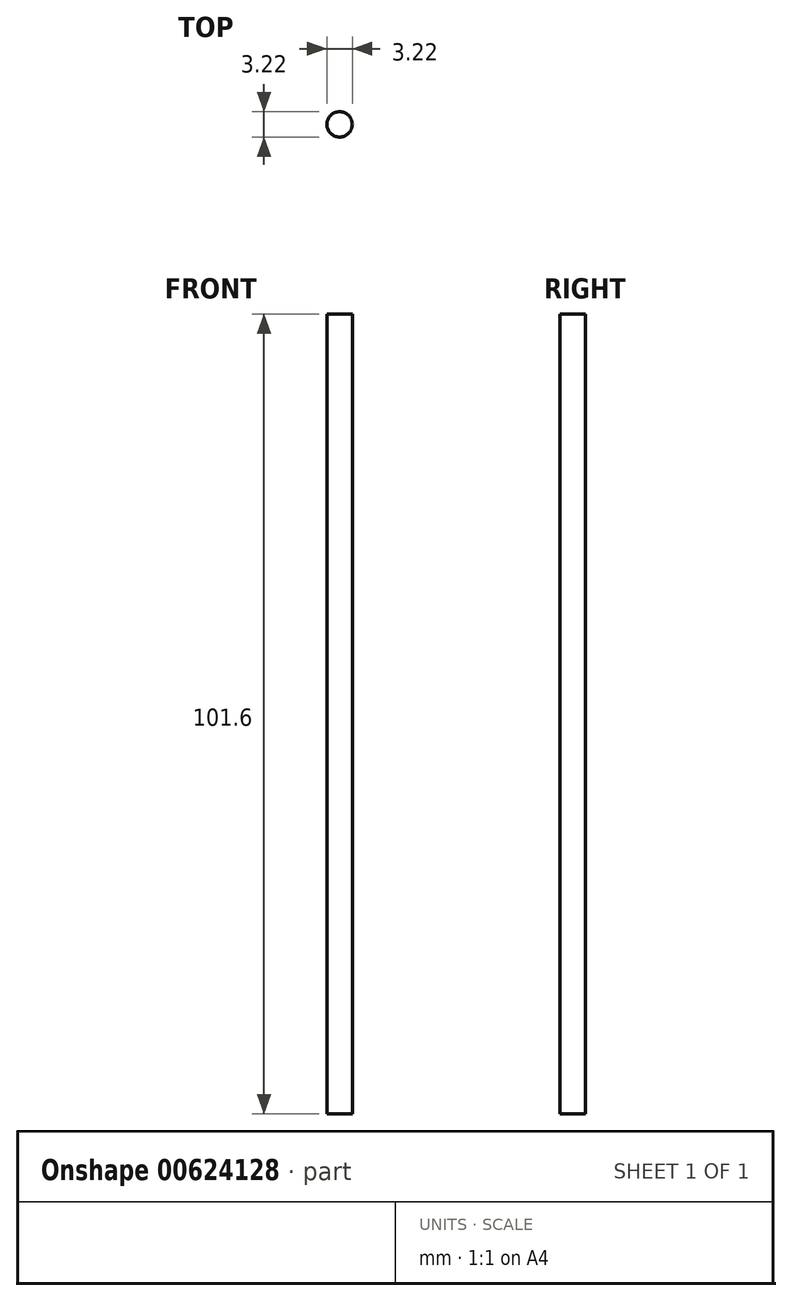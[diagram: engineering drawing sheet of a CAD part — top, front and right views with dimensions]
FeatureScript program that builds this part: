
annotation { "Feature Type Name" : "Feature", "Feature Type Description" : "" }
export const myFeature = defineFeature(function(context is Context, id is Id, definition is map)
    precondition{}
    {
        {
            var Q0;
            Q0=qCreatedBy(makeId("Top.planeOp"),FACE);
            var sketch = newSketch(context, id + "F0", { "sketchPlane" : qUnion([Q0])});
            skCircle(sketch, "E0", {"center": v(0, 0) * mm, "radius": 1.61 * mm});
            skSolve(sketch);
        }
        {
            var Q0;
            Q0 = qSketchRegion(id + "F0", true);
            extrude(context, id + "F1", {"entities" : qUnion([Q0]), "depth" : 101.6 * mm, "offsetDistance" : 25.4 * mm});
        }
    });
